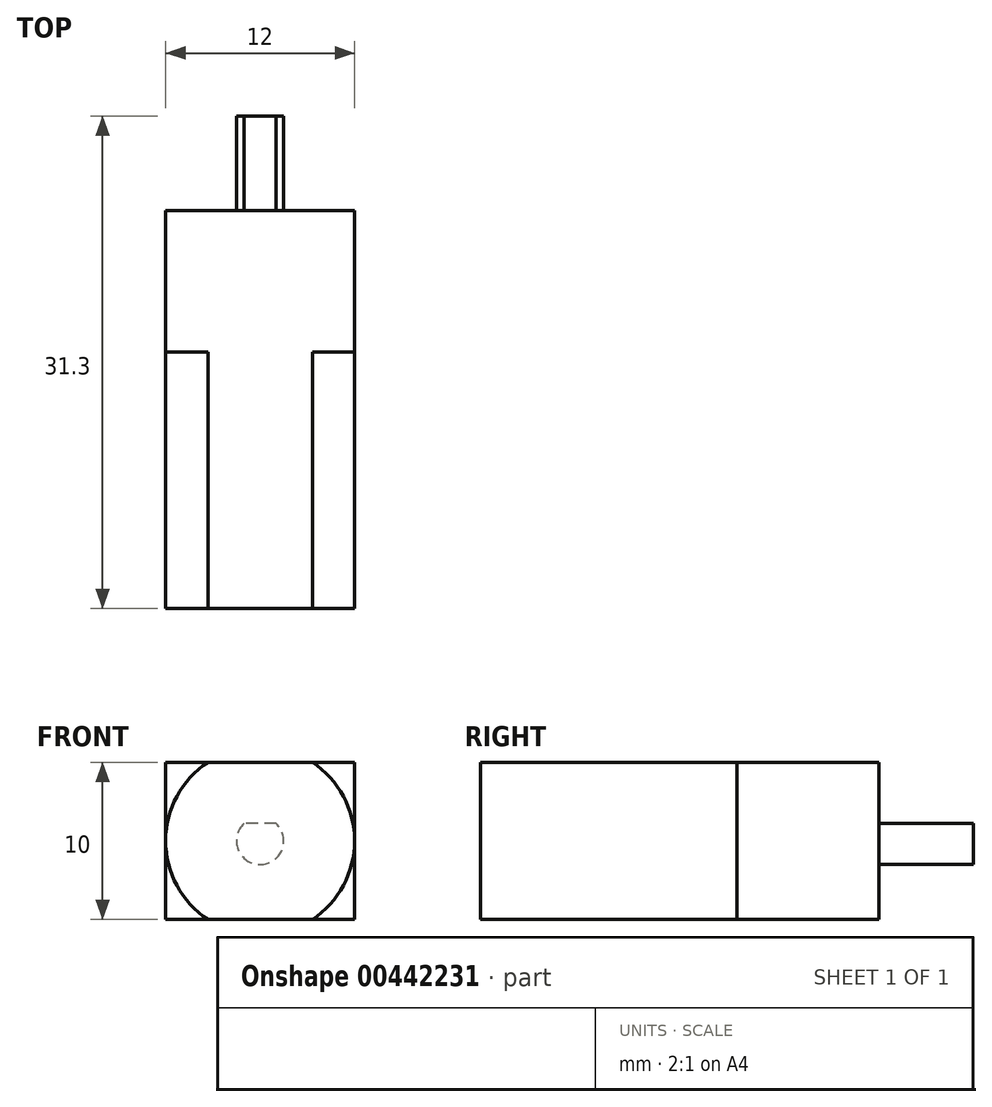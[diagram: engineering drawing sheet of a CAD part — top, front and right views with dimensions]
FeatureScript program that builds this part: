
annotation { "Feature Type Name" : "Feature", "Feature Type Description" : "" }
export const myFeature = defineFeature(function(context is Context, id is Id, definition is map)
    precondition{}
    {
        {
            var Q0;
            Q0=qCreatedBy(makeId("Front.planeOp"),FACE);
            var sketch = newSketch(context, id + "F0", { "sketchPlane" : qUnion([Q0])});
            skLineSegment(sketch, "E0.bottom", {"start": v(6, -5) * mm, "end": v(-6, -5) * mm});
            skLineSegment(sketch, "E0.top", {"start": v(6, 5) * mm, "end": v(-6, 5) * mm});
            skLineSegment(sketch, "E0.left", {"start": v(6, -5) * mm, "end": v(6, 5) * mm});
            skLineSegment(sketch, "E0.right", {"start": v(-6, -5) * mm, "end": v(-6, 5) * mm});
            skPoint(sketch, "E0.middle", {"position": v(0, 0) * mm});
            skSolve(sketch);
        }
        {
            var Q0;
            Q0 = qSketchRegion(id + "F0", true);
            extrude(context, id + "F1", {"entities" : qUnion([Q0]), "depth" : 9 * mm});
        }
        {
            var Q0;
            Q0=makeQuery(id+"F1.opExtrude","CAP_FACE",FACE,{"disambiguationData":[OSD([sQuery(id+"F0.wireOp",EDGE,"E0.bottom"),sQuery(id+"F0.wireOp",EDGE,"E0.top"),sQuery(id+"F0.wireOp",EDGE,"E0.left"),sQuery(id+"F0.wireOp",EDGE,"E0.right")])],"isStart":false});
            var sketch = newSketch(context, id + "F2", { "sketchPlane" : qUnion([Q0])});
            skArc(sketch, "E1", {"start": v(-3.32, 5) * mm, "mid": v(-6, 0) * mm, "end": v(-3.32, -5) * mm});
            skLineSegment(sketch, "E2", {"start": v(3.32, 5) * mm, "end": v(-3.32, 5) * mm});
            skLineSegment(sketch, "E3", {"start": v(-3.32, -5) * mm, "end": v(3.32, -5) * mm});
            skArc(sketch, "E4.MirrorCS", {"start": v(3.32, 5) * mm, "mid": v(6, 0) * mm, "end": v(3.32, -5) * mm});
            skSolve(sketch);
        }
        {
            var Q0;
            Q0 = qSketchRegion(id + "F2", true);
            extrude(context, id + "F3", {"entities" : qUnion([Q0]), "operationType" : NewBodyOperationType.ADD, "depth" : 16.3 * mm});
        }
        {
            var Q0;
            Q0=makeQuery(id+"F1.opExtrude","CAP_FACE",FACE,{"disambiguationData":[OSD([sQuery(id+"F0.wireOp",EDGE,"E0.bottom"),sQuery(id+"F0.wireOp",EDGE,"E0.top"),sQuery(id+"F0.wireOp",EDGE,"E0.left"),sQuery(id+"F0.wireOp",EDGE,"E0.right")])],"isStart":true});
            var sketch = newSketch(context, id + "F4", { "sketchPlane" : qUnion([Q0])});
            skArc(sketch, "E5", {"start": v(-1.02, 1.1) * mm, "mid": v(0, -1.5) * mm, "end": v(1.02, 1.1) * mm});
            skLineSegment(sketch, "E6", {"start": v(-1.02, 1.1) * mm, "end": v(1.02, 1.1) * mm});
            skSolve(sketch);
        }
        {
            var Q0;
            Q0 = qSketchRegion(id + "F4", true);
            extrude(context, id + "F5", {"entities" : qUnion([Q0]), "operationType" : NewBodyOperationType.ADD, "depth" : 6 * mm});
        }
    });
